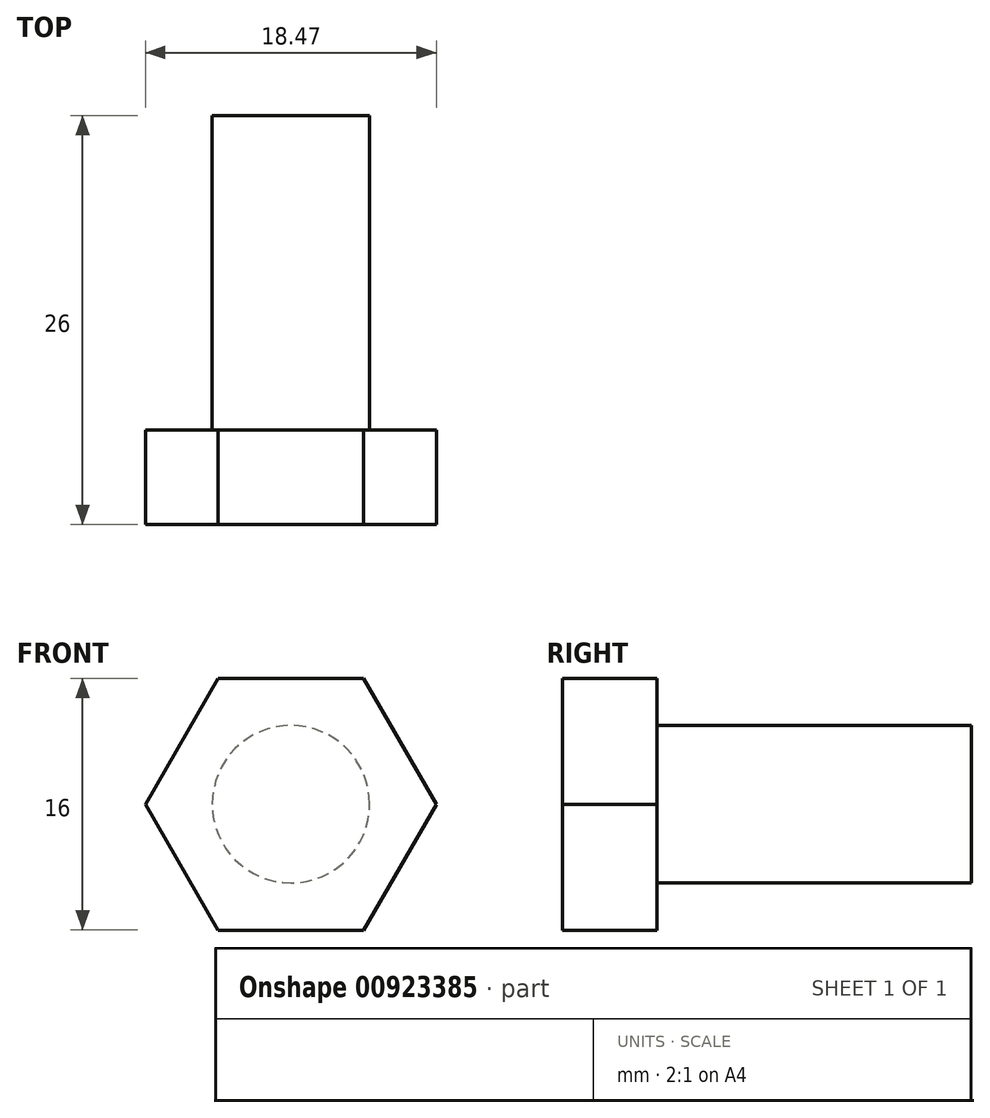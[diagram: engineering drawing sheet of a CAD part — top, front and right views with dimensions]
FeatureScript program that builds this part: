
annotation { "Feature Type Name" : "Feature", "Feature Type Description" : "" }
export const myFeature = defineFeature(function(context is Context, id is Id, definition is map)
    precondition{}
    {
        {
            var Q0;
            Q0=qCreatedBy(makeId("Front.planeOp"),FACE);
            var sketch = newSketch(context, id + "F0", { "sketchPlane" : qUnion([Q0])});
            skCircle(sketch, "E0.cCircle", {"center": v(-57.85, 58.03) * mm, "radius": 8 * mm, "construction": true});
            skLineSegment(sketch, "E0.0", {"start": v(-62.47, 66.03) * mm, "end": v(-53.24, 66.03) * mm});
            skLineSegment(sketch, "E0.1", {"start": v(-53.24, 66.03) * mm, "end": v(-48.62, 58.03) * mm});
            skLineSegment(sketch, "E0.2", {"start": v(-48.62, 58.03) * mm, "end": v(-53.24, 50.03) * mm});
            skLineSegment(sketch, "E0.3", {"start": v(-53.24, 50.03) * mm, "end": v(-62.47, 50.03) * mm});
            skLineSegment(sketch, "E0.4", {"start": v(-62.47, 50.03) * mm, "end": v(-67.1, 58.03) * mm});
            skLineSegment(sketch, "E0.5", {"start": v(-67.1, 58.03) * mm, "end": v(-62.47, 66.03) * mm});
            skPoint(sketch, "E0.0.midPoint", {"position": v(-57.85, 66.03) * mm});
            skSolve(sketch);
        }
        {
            var Q0;
            Q0 = qSketchRegion(id + "F0", true);
            extrude(context, id + "F1", {"entities" : qUnion([Q0]), "depth" : 6 * mm, "offsetDistance" : 25 * mm});
        }
        {
            var Q0;
            Q0=makeQuery(id+"F1.opExtrude","CAP_FACE",FACE,{"disambiguationData":[OSD([sQuery(id+"F0.wireOp",EDGE,"E0.0"),sQuery(id+"F0.wireOp",EDGE,"E0.1"),sQuery(id+"F0.wireOp",EDGE,"E0.2"),sQuery(id+"F0.wireOp",EDGE,"E0.3"),sQuery(id+"F0.wireOp",EDGE,"E0.4"),sQuery(id+"F0.wireOp",EDGE,"E0.5")])],"isStart":true});
            var sketch = newSketch(context, id + "F2", { "sketchPlane" : qUnion([Q0])});
            skCircle(sketch, "E1", {"center": v(57.85, 58.03) * mm, "radius": 5 * mm});
            skPoint(sketch, "E1.centerSnap0", {"position": v(57.85, 66.03) * mm});
            skSolve(sketch);
        }
        {
            var Q0;
            Q0=makeQuery(id+"F2.imprint","IMPRINT",FACE,{"disambiguationData":[TD([[makeQuery(id+"F2.imprint","IMPRINT",EDGE,{"derivedFrom":sQuery(id+"F2.wireOp",EDGE,"E1")}),1.0]])]});
            extrude(context, id + "F3", {"entities" : qUnion([Q0]), "operationType" : NewBodyOperationType.ADD, "depth" : 20 * mm, "offsetDistance" : 25 * mm});
        }
    });
